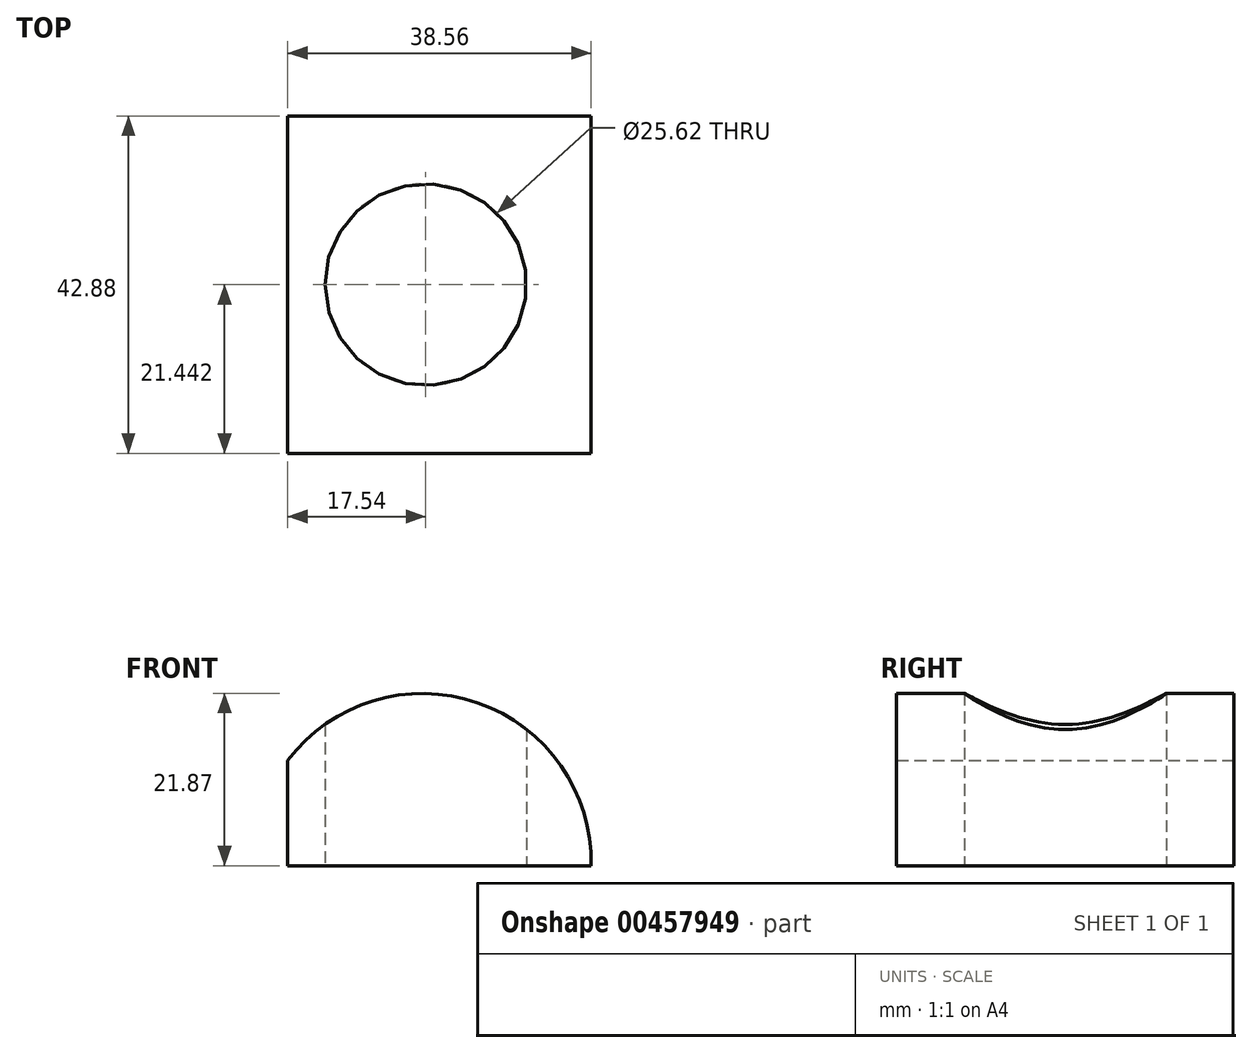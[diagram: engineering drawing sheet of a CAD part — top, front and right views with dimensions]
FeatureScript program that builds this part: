
annotation { "Feature Type Name" : "Feature", "Feature Type Description" : "" }
export const myFeature = defineFeature(function(context is Context, id is Id, definition is map)
    precondition{}
    {
        {
            var Q0;
            Q0=qCreatedBy(makeId("Front.planeOp"),FACE);
            var sketch = newSketch(context, id + "F0", { "sketchPlane" : qUnion([Q0])});
            skLineSegment(sketch, "E0", {"start": v(-21.86, 0) * mm, "end": v(21.01, 0) * mm});
            skArc(sketch, "E1", {"start": v(21.01, 0) * mm, "mid": v(-0.43, 21.87) * mm, "end": v(-21.86, 0) * mm});
            skSolve(sketch);
        }
        {
            var Q0;
            Q0=makeQuery(id+"F0.imprint","IMPRINT",FACE,{"disambiguationData":[TD([[makeQuery(id+"F0.imprint","IMPRINT",EDGE,{"derivedFrom":sQuery(id+"F0.wireOp",EDGE,"E0")}),1.0]])]});
            extrude(context, id + "F1", {"entities" : qUnion([Q0]), "depth" : 42.88 * mm, "offsetDistance" : 25.4 * mm});
        }
        {
            var Q0;
            Q0=makeQuery(id+"F1.opExtrude","SWEPT_FACE",FACE,{"disambiguationData":[OSD([sQuery(id+"F0.wireOp",EDGE,"E0")])]});
            var sketch = newSketch(context, id + "F2", { "sketchPlane" : qUnion([Q0])});
            skPoint(sketch, "E2", {"position": v(0, 42.88) * mm});
            skPoint(sketch, "E3", {"position": v(-21.86, 21.44) * mm});
            skPoint(sketch, "E4", {"position": v(21.01, 21.44) * mm});
            skPoint(sketch, "E5", {"position": v(0, 21.44) * mm});
            skCircle(sketch, "E6", {"center": v(0, 21.44) * mm, "radius": 12.8 * mm});
            skSolve(sketch);
        }
        {
            var Q0;
            Q0=makeQuery(id+"F2.imprint","IMPRINT",FACE,{"disambiguationData":[TD([[makeQuery(id+"F2.imprint","IMPRINT",EDGE,{"derivedFrom":sQuery(id+"F2.wireOp",EDGE,"E6")}),1.0]])]});
            extrude(context, id + "F3", {"entities" : qUnion([Q0]), "operationType" : NewBodyOperationType.REMOVE, "oppositeDirection" : true, "depth" : 25.4 * mm, "offsetDistance" : 25.4 * mm});
        }
        {
            var Q0;
            Q0=makeQuery(id+"F1.opExtrude","SWEPT_FACE",FACE,{"disambiguationData":[OSD([sQuery(id+"F0.wireOp",EDGE,"E0")])]});
            var sketch = newSketch(context, id + "F4", { "sketchPlane" : qUnion([Q0])});
            skLineSegment(sketch, "E7", {"start": v(-17.54, 0) * mm, "end": v(-17.54, 42.88) * mm});
            skLineSegment(sketch, "E8", {"start": v(-17.54, 42.88) * mm, "end": v(-25.82, 47.95) * mm});
            skLineSegment(sketch, "E9", {"start": v(-25.82, 47.95) * mm, "end": v(-25.82, -20.26) * mm});
            skLineSegment(sketch, "E10", {"start": v(-25.82, -20.26) * mm, "end": v(-17.54, 0) * mm});
            skSolve(sketch);
        }
        {
            var Q0;
            {var subQ0=sQuery(id+"F4.wireOp",EDGE,"E7");Q0=makeQuery(id+"F4.imprint","IMPRINT",FACE,{"disambiguationData":[TD([[makeQuery(id+"F4.imprint","IMPRINT",EDGE,{"derivedFrom":subQ0}),1.0]])]});}
            extrude(context, id + "F5", {"entities" : qUnion([Q0]), "operationType" : NewBodyOperationType.REMOVE, "oppositeDirection" : true, "depth" : 25.4 * mm, "offsetDistance" : 25.4 * mm});
        }
        {
            var Q0;
            Q0=makeQuery(id+"F5.boolean.opBoolean","COPY",FACE,{"derivedFrom":makeQuery(id+"F5.opExtrude","SWEPT_FACE",FACE,{"disambiguationData":[OSD([sQuery(id+"F0.wireOp",EDGE,"E0"),sQuery(id+"F0.wireOp",EDGE,"E1")])]})});
            var sketch = newSketch(context, id + "F6", { "sketchPlane" : qUnion([Q0])});
            skSolve(sketch);
        }
        {
            var Q0;
            {var subQ0=sQuery(id+"F0.wireOp",EDGE,"E1");var subQ1=sQuery(id+"F0.wireOp",EDGE,"E0");Q0=makeQuery(id+"F6.imprint","IMPRINT",FACE,{"disambiguationData":[TD([[makeQuery(id+"F6.imprint","IMPRINT",EDGE,{"derivedFrom":makeQuery(id+"F5.boolean.opBoolean","INTERSECT",EDGE,{"derivedFrom":[makeQuery(id+"F1.opExtrude","SWEPT_FACE",FACE,{"disambiguationData":[OSD([subQ0])]}),makeQuery(id+"F5.opExtrude","SWEPT_FACE",FACE,{"disambiguationData":[OSD([subQ1,subQ0])]})]})}),-1.0]])]});}
            extrude(context, id + "F7", {"entities" : qUnion([Q0]), "operationType" : NewBodyOperationType.REMOVE, "oppositeDirection" : true, "depth" : 25.4 * mm, "offsetDistance" : 25.4 * mm});
        }
    });
